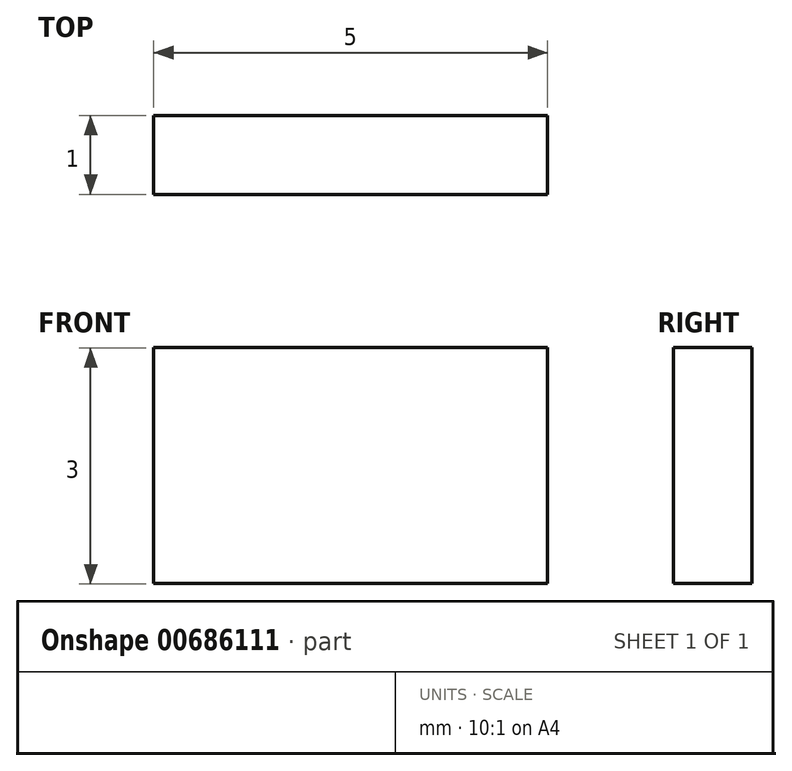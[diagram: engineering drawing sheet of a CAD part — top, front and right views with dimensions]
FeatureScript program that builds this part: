
annotation { "Feature Type Name" : "Feature", "Feature Type Description" : "" }
export const myFeature = defineFeature(function(context is Context, id is Id, definition is map)
    precondition{}
    {
        {
            var Q0;
            Q0=qCreatedBy(makeId("Front.planeOp"),FACE);
            var sketch = newSketch(context, id + "F0", { "sketchPlane" : qUnion([Q0])});
            skLineSegment(sketch, "E0.bottom", {"start": v(-45.23, 32.16) * mm, "end": v(-40.23, 32.16) * mm});
            skLineSegment(sketch, "E0.top", {"start": v(-45.23, 29.16) * mm, "end": v(-40.23, 29.16) * mm});
            skLineSegment(sketch, "E0.left", {"start": v(-45.23, 32.16) * mm, "end": v(-45.23, 29.16) * mm});
            skLineSegment(sketch, "E0.right", {"start": v(-40.23, 32.16) * mm, "end": v(-40.23, 29.16) * mm});
            skSolve(sketch);
        }
        {
            var Q0;
            Q0=qSketchRegion(id+"F0",true);
            extrude(context, id + "F1", {"entities" : qUnion([Q0]), "depth" : 1 * mm, "offsetDistance" : 25 * mm});
        }
    });
